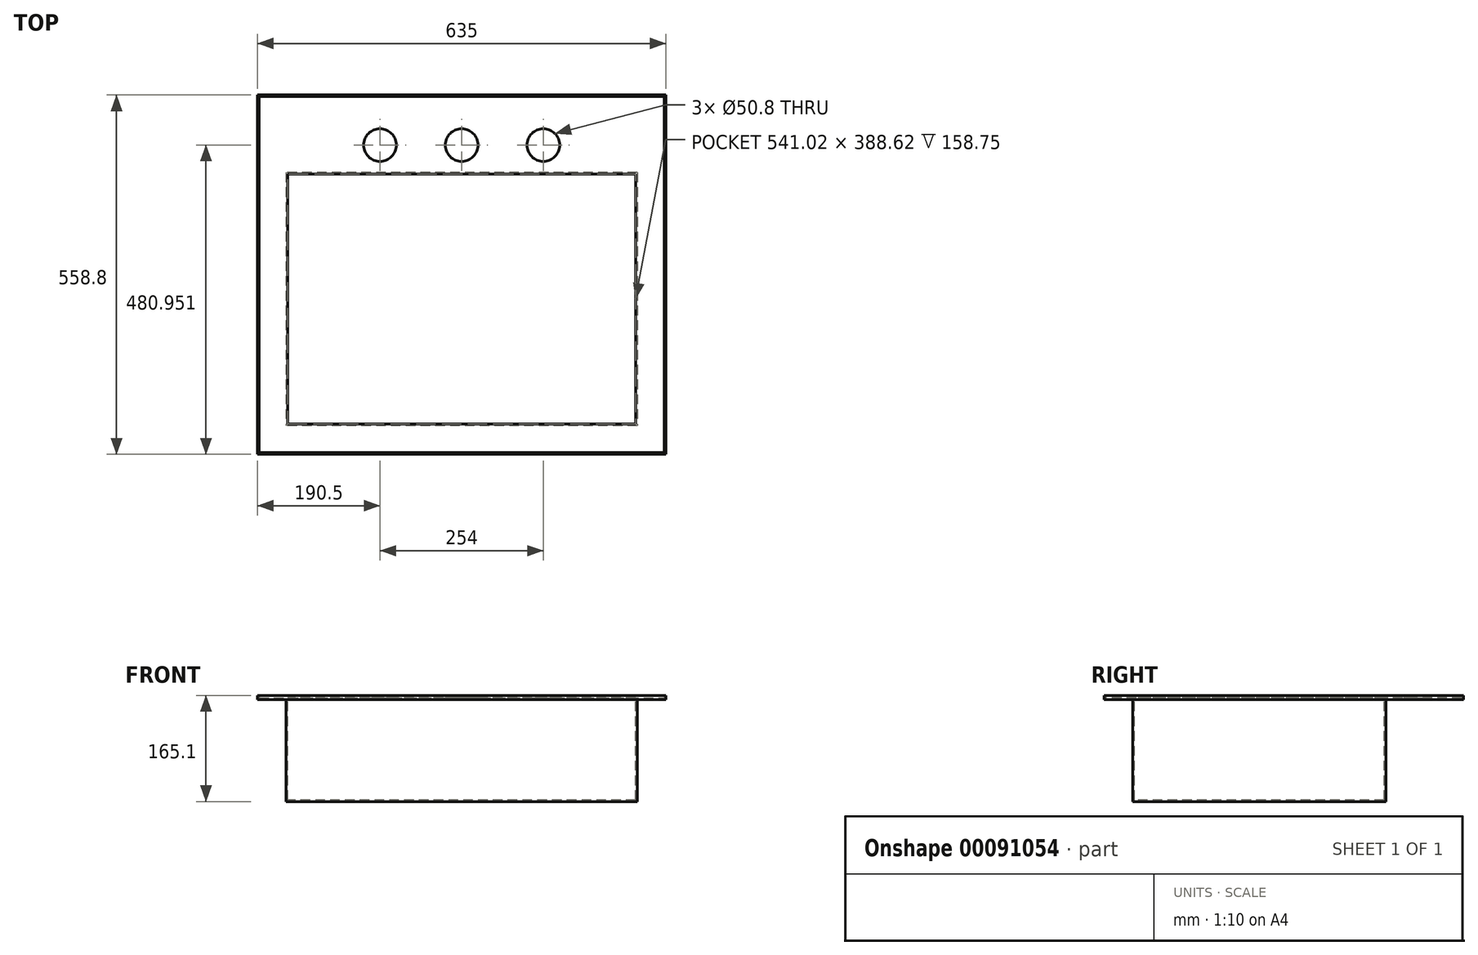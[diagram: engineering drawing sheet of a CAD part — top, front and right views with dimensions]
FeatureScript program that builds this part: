
annotation { "Feature Type Name" : "Feature", "Feature Type Description" : "" }
export const myFeature = defineFeature(function(context is Context, id is Id, definition is map)
    precondition{}
    {
        {
            var Q0;
            Q0=qCreatedBy(makeId("Top.planeOp"),FACE);
            var sketch = newSketch(context, id + "F0", { "sketchPlane" : qUnion([Q0])});
            skLineSegment(sketch, "E0.bottom", {"start": v(-469.07, 276) * mm, "end": v(165.93, 276) * mm});
            skLineSegment(sketch, "E0.top", {"start": v(-469.07, -282.8) * mm, "end": v(165.93, -282.8) * mm});
            skLineSegment(sketch, "E0.left", {"start": v(-469.07, 276) * mm, "end": v(-469.07, -282.8) * mm});
            skLineSegment(sketch, "E0.right", {"start": v(165.93, 276) * mm, "end": v(165.93, -282.8) * mm});
            skSolve(sketch);
        }
        {
            var Q0;
            Q0 = qSketchRegion(id + "F0", true);
            extrude(context, id + "F1", {"entities" : qUnion([Q0]), "depth" : 6.35 * mm});
        }
        {
            var Q0;
            Q0=makeQuery(id+"F1.opExtrude","CAP_FACE",FACE,{"disambiguationData":[OSD([sQuery(id+"F0.wireOp",EDGE,"E0.bottom"),sQuery(id+"F0.wireOp",EDGE,"E0.top"),sQuery(id+"F0.wireOp",EDGE,"E0.left"),sQuery(id+"F0.wireOp",EDGE,"E0.right")])],"isStart":true});
            var sketch = newSketch(context, id + "F2", { "sketchPlane" : qUnion([Q0])});
            skLineSegment(sketch, "E1.bottom", {"start": v(121.48, -155.36) * mm, "end": v(-424.62, -155.36) * mm});
            skLineSegment(sketch, "E1.top", {"start": v(121.48, 238.34) * mm, "end": v(-424.62, 238.34) * mm});
            skLineSegment(sketch, "E1.left", {"start": v(121.48, -155.36) * mm, "end": v(121.48, 238.34) * mm});
            skLineSegment(sketch, "E1.right", {"start": v(-424.62, -155.36) * mm, "end": v(-424.62, 238.34) * mm});
            skLineSegment(sketch, "E2", {"start": v(-151.57, -191.03) * mm, "end": v(-151.57, 250.07) * mm, "construction": true});
            skPoint(sketch, "E2.startSnap0", {"position": v(-151.57, -155.36) * mm});
            skPoint(sketch, "E2.endSnap0", {"position": v(-151.57, 238.34) * mm});
            skCircle(sketch, "E3", {"center": v(-24.57, -198.16) * mm, "radius": 25.4 * mm});
            skCircle(sketch, "E4.1.0.0", {"center": v(-151.57, -198.16) * mm, "radius": 25.4 * mm});
            skCircle(sketch, "E4.2.0.0", {"center": v(-278.57, -198.16) * mm, "radius": 25.4 * mm});
            skLineSegment(sketch, "E4.direction1", {"start": v(-24.57, -198.16) * mm, "end": v(-151.57, -198.16) * mm, "construction": true});
            skSolve(sketch);
        }
        {
            var Q0;
            Q0=makeQuery(id+"F2.imprint","IMPRINT",FACE,{"disambiguationData":[TD([[makeQuery(id+"F2.imprint","IMPRINT",EDGE,{"derivedFrom":sQuery(id+"F2.wireOp",EDGE,"E1.bottom")}),-1.0]])]});
            extrude(context, id + "F3", {"entities" : qUnion([Q0]), "operationType" : NewBodyOperationType.ADD, "depth" : 158.75 * mm});
        }
        {
            var Q0;
            Q0=makeQuery(id+"F1.opExtrude","CAP_FACE",FACE,{"disambiguationData":[OSD([sQuery(id+"F0.wireOp",EDGE,"E0.bottom"),sQuery(id+"F0.wireOp",EDGE,"E0.top"),sQuery(id+"F0.wireOp",EDGE,"E0.left"),sQuery(id+"F0.wireOp",EDGE,"E0.right")])],"isStart":false});
            shell(context, id + "F4", {"entities" : qUnion([Q0]), "thickness" : 2.54 * mm});
        }
        {
            var Q0;
            Q0=makeQuery(id+"F2.imprint","IMPRINT",FACE,{"disambiguationData":[TD([[makeQuery(id+"F2.imprint","IMPRINT",EDGE,{"derivedFrom":sQuery(id+"F2.wireOp",EDGE,"E4.2.0.0")}),1.0]])]});
            var Q1;
            Q1=makeQuery(id+"F2.imprint","IMPRINT",FACE,{"disambiguationData":[TD([[makeQuery(id+"F2.imprint","IMPRINT",EDGE,{"derivedFrom":sQuery(id+"F2.wireOp",EDGE,"E4.1.0.0")}),1.0]])]});
            var Q2;
            Q2=makeQuery(id+"F2.imprint","IMPRINT",FACE,{"disambiguationData":[TD([[makeQuery(id+"F2.imprint","IMPRINT",EDGE,{"derivedFrom":sQuery(id+"F2.wireOp",EDGE,"E3")}),1.0]])]});
            extrude(context, id + "F5", {"entities" : qUnion([Q0, Q1, Q2]), "operationType" : NewBodyOperationType.REMOVE, "oppositeDirection" : true, "depth" : 25.4 * mm});
        }
    });
